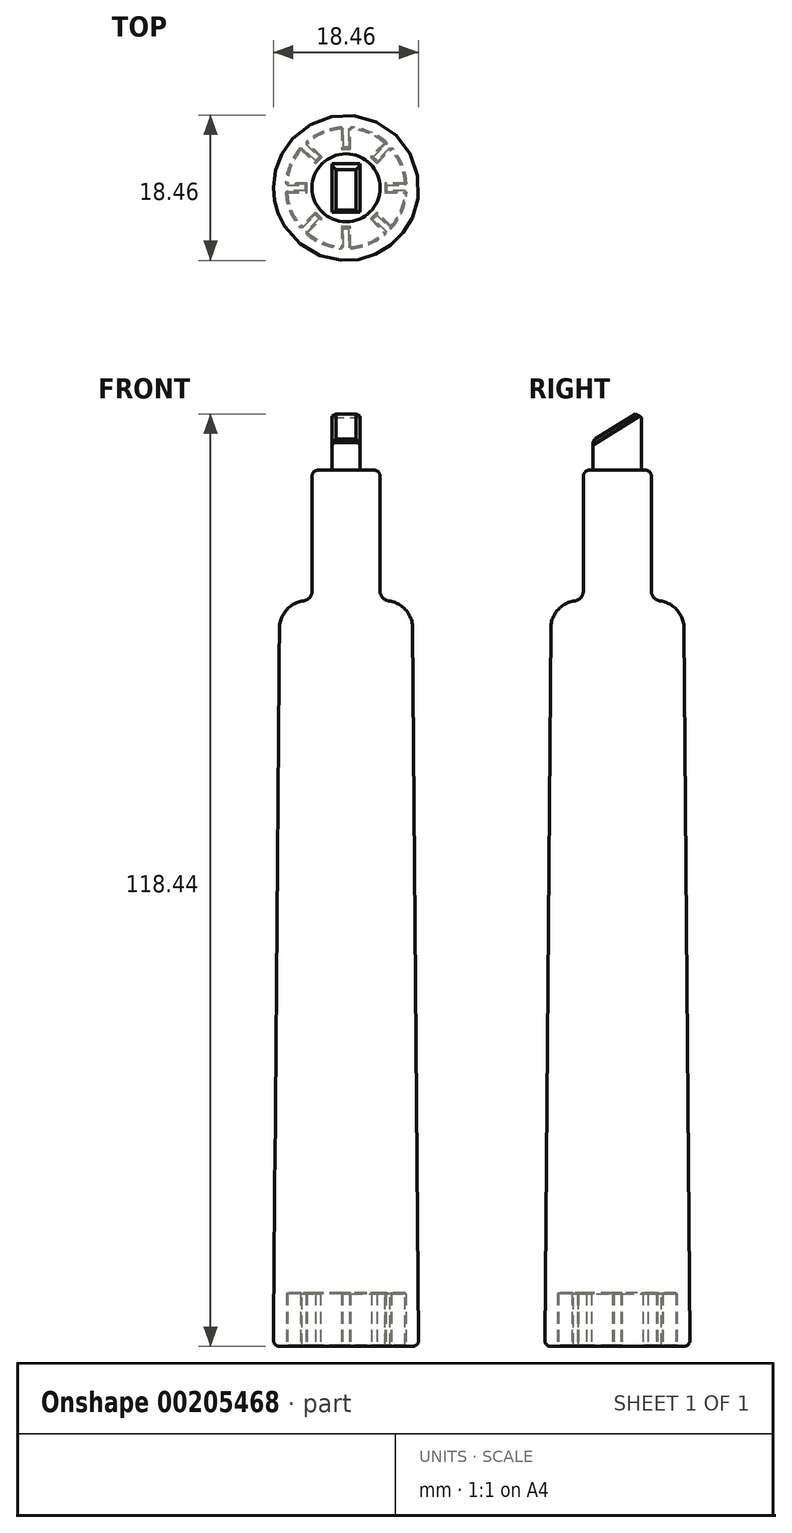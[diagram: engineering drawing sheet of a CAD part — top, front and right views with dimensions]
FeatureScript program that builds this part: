
annotation { "Feature Type Name" : "Feature", "Feature Type Description" : "" }
export const myFeature = defineFeature(function(context is Context, id is Id, definition is map)
    precondition{}
    {
        {
            var Q0;
            Q0=qCreatedBy(makeId("Front.planeOp"),FACE);
            var sketch = newSketch(context, id + "F0", { "sketchPlane" : qUnion([Q0])});
            skLineSegment(sketch, "E0", {"start": v(0, 0) * mm, "end": v(0, 111.3) * mm, "construction": true});
            skLineSegment(sketch, "E1", {"start": v(9.23, 0) * mm, "end": v(8.46, 91.26) * mm});
            skLineSegment(sketch, "E2", {"start": v(4.32, 111.3) * mm, "end": v(4.32, 95.96) * mm});
            skArc(sketch, "E3", {"start": v(8.46, 91.26) * mm, "mid": v(7.58, 93.55) * mm, "end": v(5.42, 94.7) * mm});
            skLineSegment(sketch, "E4", {"start": v(0, 111.3) * mm, "end": v(4.32, 111.3) * mm});
            skLineSegment(sketch, "E5", {"start": v(0, 0) * mm, "end": v(9.23, 0) * mm});
            skPoint(sketch, "E6.visualSharp", {"position": v(4.32, 94.67) * mm});
            skArc(sketch, "E6.filletArc", {"start": v(4.32, 95.96) * mm, "mid": v(4.63, 95.12) * mm, "end": v(5.42, 94.7) * mm});
            skLineSegment(sketch, "E7", {"start": v(0, 111.3) * mm, "end": v(0, 0) * mm});
            skSolve(sketch);
        }
        {
            var Q0;
            Q0 = qSketchRegion(id + "F0", true);
            var Q1;
            Q1=sQuery(id+"F0.wireOp",EDGE,"E0");
            revolve(context, id + "F1", {"entities" : qUnion([Q0]), "axis" : qUnion([Q1]), "revolveType" : RevolveType.FULL});
        }
        {
            var Q0;
            Q0=makeQuery(id+"F1.opRevolve","SWEPT_EDGE",EDGE,{"disambiguationData":[OSD([sQuery(id+"F0.wireOp",EDGE,"E2"),sQuery(id+"F0.wireOp",EDGE,"E4")])]});
            var Q1;
            Q1=makeQuery(id+"F1.opRevolve","SWEPT_EDGE",EDGE,{"disambiguationData":[OSD([sQuery(id+"F0.wireOp",EDGE,"E1"),sQuery(id+"F0.wireOp",EDGE,"E5")])]});
            fillet(context, id + "F2", {"entities" : qUnion([Q0, Q1]), "radius" : 0.76 * mm, "tangentPropagation" : true, "allowEdgeOverflow" : false});
        }
        {
            var Q0;
            Q0=makeQuery(id+"F1.opRevolve","SWEPT_FACE",FACE,{"disambiguationData":[OSD([sQuery(id+"F0.wireOp",EDGE,"E4")])]});
            var sketch = newSketch(context, id + "F3", { "sketchPlane" : qUnion([Q0])});
            skLineSegment(sketch, "E8.bottom", {"start": v(-1.78, 3.08) * mm, "end": v(1.78, 3.08) * mm});
            skLineSegment(sketch, "E8.top", {"start": v(-1.78, -3.08) * mm, "end": v(1.78, -3.08) * mm});
            skLineSegment(sketch, "E8.left", {"start": v(-1.78, 3.08) * mm, "end": v(-1.78, -3.08) * mm});
            skLineSegment(sketch, "E8.right", {"start": v(1.78, 3.08) * mm, "end": v(1.78, -3.08) * mm});
            skSolve(sketch);
        }
        {
            var Q0;
            Q0 = qSketchRegion(id + "F3", true);
            extrude(context, id + "F4", {"entities" : qUnion([Q0]), "operationType" : NewBodyOperationType.ADD, "depth" : 7.62 * mm});
        }
        {
            var Q0;
            Q0=makeQuery(id+"F4.opExtrude","SWEPT_FACE",FACE,{"disambiguationData":[OSD([sQuery(id+"F3.wireOp",EDGE,"E8.right")])]});
            var sketch = newSketch(context, id + "F5", { "sketchPlane" : qUnion([Q0])});
            skLineSegment(sketch, "E9", {"start": v(-3.08, 118.92) * mm, "end": v(-3.08, 115.11) * mm});
            skLineSegment(sketch, "E10", {"start": v(-3.08, 115.11) * mm, "end": v(3.08, 118.92) * mm});
            skLineSegment(sketch, "E11", {"start": v(3.08, 118.92) * mm, "end": v(-3.08, 118.92) * mm});
            skSolve(sketch);
        }
        {
            var Q0;
            Q0 = qSketchRegion(id + "F5", true);
            extrude(context, id + "F6", {"entities" : qUnion([Q0]), "operationType" : NewBodyOperationType.REMOVE, "endBound" : BoundingType.UP_TO_NEXT, "oppositeDirection" : true, "depth" : 25.4 * mm});
        }
        {
            var Q0;
            Q0=makeQuery(id+"F6.boolean.opBoolean","COPY",FACE,{"derivedFrom":makeQuery(id+"F6.opExtrude","SWEPT_FACE",FACE,{"disambiguationData":[OSD([sQuery(id+"F5.wireOp",EDGE,"E10")])]})});
            chamfer(context, id + "F7", {"entities" : qUnion([Q0]), "width" : 0.5 * mm, "tangentPropagation" : true});
        }
        {
            var Q0;
            Q0=makeQuery(id+"F1.opRevolve","SWEPT_FACE",FACE,{"disambiguationData":[OSD([sQuery(id+"F0.wireOp",EDGE,"E5")])]});
            var sketch = newSketch(context, id + "F8", { "sketchPlane" : qUnion([Q0])});
            skArc(sketch, "E12", {"start": v(-7.6, -0.46) * mm, "mid": v(-7.04, -2.92) * mm, "end": v(-5.7, -5.06) * mm});
            skLineSegment(sketch, "E13", {"start": v(-7.6, -0.46) * mm, "end": v(-5.07, -0.46) * mm});
            skLineSegment(sketch, "E14", {"start": v(-5.07, -0.46) * mm, "end": v(-5.07, 0.46) * mm});
            skLineSegment(sketch, "E15", {"start": v(-5.07, 0.46) * mm, "end": v(-7.6, 0.46) * mm});
            skLineSegment(sketch, "E16", {"start": v(7.62, 0) * mm, "end": v(-7.6, 0) * mm, "construction": true});
            skLineSegment(sketch, "E17.1.0", {"start": v(-3.26, 3.9) * mm, "end": v(-5.06, 5.7) * mm});
            skLineSegment(sketch, "E17.1.1", {"start": v(-3.9, 3.26) * mm, "end": v(-3.26, 3.9) * mm});
            skLineSegment(sketch, "E17.1.2", {"start": v(-5.7, 5.06) * mm, "end": v(-3.9, 3.26) * mm});
            skLineSegment(sketch, "E17.2.0", {"start": v(0.46, 5.07) * mm, "end": v(0.46, 7.6) * mm});
            skLineSegment(sketch, "E17.2.1", {"start": v(-0.46, 5.07) * mm, "end": v(0.46, 5.07) * mm});
            skLineSegment(sketch, "E17.2.2", {"start": v(-0.46, 7.6) * mm, "end": v(-0.46, 5.07) * mm});
            skLineSegment(sketch, "E17.3.0", {"start": v(3.9, 3.26) * mm, "end": v(5.7, 5.06) * mm});
            skLineSegment(sketch, "E17.3.1", {"start": v(3.26, 3.9) * mm, "end": v(3.9, 3.26) * mm});
            skLineSegment(sketch, "E17.3.2", {"start": v(5.06, 5.7) * mm, "end": v(3.26, 3.9) * mm});
            skLineSegment(sketch, "E17.4.0", {"start": v(5.07, -0.46) * mm, "end": v(7.6, -0.46) * mm});
            skLineSegment(sketch, "E17.4.1", {"start": v(5.07, 0.46) * mm, "end": v(5.07, -0.46) * mm});
            skLineSegment(sketch, "E17.4.2", {"start": v(7.6, 0.46) * mm, "end": v(5.07, 0.46) * mm});
            skLineSegment(sketch, "E17.5.0", {"start": v(3.26, -3.9) * mm, "end": v(5.06, -5.7) * mm});
            skLineSegment(sketch, "E17.5.1", {"start": v(3.9, -3.26) * mm, "end": v(3.26, -3.9) * mm});
            skLineSegment(sketch, "E17.5.2", {"start": v(5.7, -5.06) * mm, "end": v(3.9, -3.26) * mm});
            skLineSegment(sketch, "E17.6.0", {"start": v(-0.46, -5.07) * mm, "end": v(-0.46, -7.6) * mm});
            skLineSegment(sketch, "E17.6.1", {"start": v(0.46, -5.07) * mm, "end": v(-0.46, -5.07) * mm});
            skLineSegment(sketch, "E17.6.2", {"start": v(0.46, -7.6) * mm, "end": v(0.46, -5.07) * mm});
            skLineSegment(sketch, "E17.7.0", {"start": v(-3.9, -3.26) * mm, "end": v(-5.7, -5.06) * mm});
            skLineSegment(sketch, "E17.7.1", {"start": v(-3.26, -3.9) * mm, "end": v(-3.9, -3.26) * mm});
            skLineSegment(sketch, "E17.7.2", {"start": v(-5.06, -5.7) * mm, "end": v(-3.26, -3.9) * mm});
            skLineSegment(sketch, "E17.anchor1", {"start": v(0, 0) * mm, "end": v(-7.6, 0.46) * mm, "construction": true});
            skLineSegment(sketch, "E17.anchor2", {"start": v(0, 0) * mm, "end": v(-5.7, -5.06) * mm, "construction": true});
            skArc(sketch, "E18.trimOffspring", {"start": v(-0.46, 7.6) * mm, "mid": v(-2.92, 7.04) * mm, "end": v(-5.06, 5.7) * mm});
            skArc(sketch, "E19.trimOffspring", {"start": v(-5.7, 5.06) * mm, "mid": v(-7.04, 2.92) * mm, "end": v(-7.6, 0.46) * mm});
            skArc(sketch, "E20.trimOffspring", {"start": v(5.06, 5.7) * mm, "mid": v(2.92, 7.04) * mm, "end": v(0.46, 7.6) * mm});
            skArc(sketch, "E21.trimOffspring", {"start": v(7.6, 0.46) * mm, "mid": v(7.04, 2.92) * mm, "end": v(5.7, 5.06) * mm});
            skArc(sketch, "E22.trimOffspring", {"start": v(5.7, -5.06) * mm, "mid": v(7.04, -2.92) * mm, "end": v(7.6, -0.46) * mm});
            skArc(sketch, "E23.trimOffspring", {"start": v(0.46, -7.6) * mm, "mid": v(2.92, -7.04) * mm, "end": v(5.06, -5.7) * mm});
            skArc(sketch, "E24.trimOffspring", {"start": v(-5.06, -5.7) * mm, "mid": v(-2.92, -7.04) * mm, "end": v(-0.46, -7.6) * mm});
            skSolve(sketch);
        }
        {
            var Q0;
            Q0 = qSketchRegion(id + "F8", true);
            extrude(context, id + "F9", {"entities" : qUnion([Q0]), "operationType" : NewBodyOperationType.REMOVE, "oppositeDirection" : true, "depth" : 6.8 * mm});
        }
        {
            var Q0;
            Q0=makeQuery(id+"F1.opRevolve","SWEPT_FACE",FACE,{"disambiguationData":[OSD([sQuery(id+"F0.wireOp",EDGE,"E5")])]});
            var Q1;
            Q1=makeQuery(id+"F9.boolean.opBoolean","COPY",FACE,{"derivedFrom":makeQuery(id+"F9.opExtrude","CAP_FACE",FACE,{"disambiguationData":[OSD([sQuery(id+"F8.wireOp",EDGE,"E12"),sQuery(id+"F8.wireOp",EDGE,"E13"),sQuery(id+"F8.wireOp",EDGE,"E14"),sQuery(id+"F8.wireOp",EDGE,"E15"),sQuery(id+"F8.wireOp",EDGE,"E17.1.0"),sQuery(id+"F8.wireOp",EDGE,"E17.1.1"),sQuery(id+"F8.wireOp",EDGE,"E17.1.2"),sQuery(id+"F8.wireOp",EDGE,"E17.2.0"),sQuery(id+"F8.wireOp",EDGE,"E17.2.1"),sQuery(id+"F8.wireOp",EDGE,"E17.2.2"),sQuery(id+"F8.wireOp",EDGE,"E17.3.0"),sQuery(id+"F8.wireOp",EDGE,"E17.3.1"),sQuery(id+"F8.wireOp",EDGE,"E17.3.2"),sQuery(id+"F8.wireOp",EDGE,"E17.4.0"),sQuery(id+"F8.wireOp",EDGE,"E17.4.1"),sQuery(id+"F8.wireOp",EDGE,"E17.4.2"),sQuery(id+"F8.wireOp",EDGE,"E17.5.0"),sQuery(id+"F8.wireOp",EDGE,"E17.5.1"),sQuery(id+"F8.wireOp",EDGE,"E17.5.2"),sQuery(id+"F8.wireOp",EDGE,"E17.6.0"),sQuery(id+"F8.wireOp",EDGE,"E17.6.1"),sQuery(id+"F8.wireOp",EDGE,"E17.6.2"),sQuery(id+"F8.wireOp",EDGE,"E17.7.0"),sQuery(id+"F8.wireOp",EDGE,"E17.7.1"),sQuery(id+"F8.wireOp",EDGE,"E17.7.2"),sQuery(id+"F8.wireOp",EDGE,"E18.trimOffspring"),sQuery(id+"F8.wireOp",EDGE,"E19.trimOffspring"),sQuery(id+"F8.wireOp",EDGE,"E20.trimOffspring"),sQuery(id+"F8.wireOp",EDGE,"E21.trimOffspring"),sQuery(id+"F8.wireOp",EDGE,"E22.trimOffspring"),sQuery(id+"F8.wireOp",EDGE,"E23.trimOffspring"),sQuery(id+"F8.wireOp",EDGE,"E24.trimOffspring")])],"isStart":false})});
            var Q2;
            Q2=makeQuery(id+"F9.boolean.opBoolean","COPY",FACE,{"derivedFrom":makeQuery(id+"F9.opExtrude","SWEPT_FACE",FACE,{"disambiguationData":[OSD([sQuery(id+"F8.wireOp",EDGE,"E12")])]})});
            var Q3;
            Q3=makeQuery(id+"F9.boolean.opBoolean","COPY",FACE,{"derivedFrom":makeQuery(id+"F9.opExtrude","SWEPT_FACE",FACE,{"disambiguationData":[OSD([sQuery(id+"F8.wireOp",EDGE,"E24.trimOffspring")])]})});
            var Q4;
            Q4=makeQuery(id+"F9.boolean.opBoolean","COPY",EDGE,{"derivedFrom":makeQuery(id+"F9.opExtrude","SWEPT_EDGE",EDGE,{"disambiguationData":[OSD([sQuery(id+"F8.wireOp",EDGE,"E17.6.2"),sQuery(id+"F8.wireOp",EDGE,"E23.trimOffspring")])]})});
            var Q5;
            Q5=makeQuery(id+"F9.boolean.opBoolean","COPY",FACE,{"derivedFrom":makeQuery(id+"F9.opExtrude","SWEPT_FACE",FACE,{"disambiguationData":[OSD([sQuery(id+"F8.wireOp",EDGE,"E22.trimOffspring")])]})});
            var Q6;
            Q6=makeQuery(id+"F9.boolean.opBoolean","COPY",EDGE,{"derivedFrom":makeQuery(id+"F9.opExtrude","SWEPT_EDGE",EDGE,{"disambiguationData":[OSD([sQuery(id+"F8.wireOp",EDGE,"E17.4.2"),sQuery(id+"F8.wireOp",EDGE,"E21.trimOffspring")])]})});
            var Q7;
            Q7=makeQuery(id+"F9.boolean.opBoolean","COPY",FACE,{"derivedFrom":makeQuery(id+"F9.opExtrude","SWEPT_FACE",FACE,{"disambiguationData":[OSD([sQuery(id+"F8.wireOp",EDGE,"E20.trimOffspring")])]})});
            var Q8;
            Q8=makeQuery(id+"F9.boolean.opBoolean","COPY",FACE,{"derivedFrom":makeQuery(id+"F9.opExtrude","SWEPT_FACE",FACE,{"disambiguationData":[OSD([sQuery(id+"F8.wireOp",EDGE,"E18.trimOffspring")])]})});
            var Q9;
            Q9=makeQuery(id+"F9.boolean.opBoolean","COPY",FACE,{"derivedFrom":makeQuery(id+"F9.opExtrude","SWEPT_FACE",FACE,{"disambiguationData":[OSD([sQuery(id+"F8.wireOp",EDGE,"E19.trimOffspring")])]})});
            chamfer(context, id + "F10", {"entities" : qUnion([Q0, Q1, Q2, Q3, Q4, Q5, Q6, Q7, Q8, Q9]), "width" : 0.13 * mm, "tangentPropagation" : true});
        }
    });
